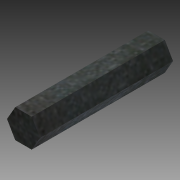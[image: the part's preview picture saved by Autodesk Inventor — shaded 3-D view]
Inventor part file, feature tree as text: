
AUTODESK INVENTOR PART (.ipt)
format: ipt  version: 2014 (Build 180170000, 170)  size: 87,552 bytes
history: native  units: in
note: dims shown in document units (in); Inventor stores cm internally (conversion verified against a paired STEP export)
features: extrude x1, sketch x1
ambient origin geometry x8: Origin, YZ Plane, XZ Plane, XY Plane, X Axis, Y Axis, Z Axis, Center Point
bodies: Solid1 (feature_tree)
feature tree (2):
  extrude  "Extrusion1"  Depth=1.75in TaperAngle=0.0deg
  sketch  "Sketch1"  dims[d0=0.375in d1=1.75in d2=0.0in]
